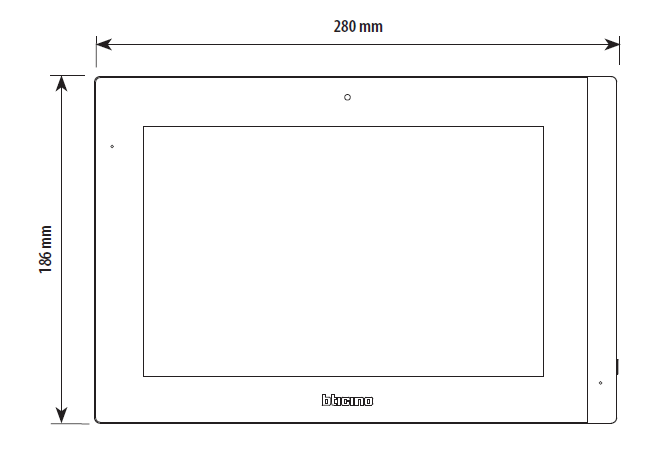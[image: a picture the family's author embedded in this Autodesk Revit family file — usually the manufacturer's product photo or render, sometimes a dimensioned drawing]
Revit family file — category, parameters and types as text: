
# Revit family: Legrand-Hotel_UX_ONE-Thermostat-Avec Service
name_source: partatom
category: Equipement électrique
units: mm (PartAtom-declared; Revit-internal decimal feet)

## family parameters
Configuration du panneau = Deux colonnes, circuits au sein
Cote de connecteur circulaire = Utiliser le diamètre
Couper avec des vides une fois chargée = Non
Hôte = Face
Partagée = Non
Point de calcul de pièce = Non
Type d'élément = Tableau de raccordement

## types (8) — shared parameters
Avec affichage = Oui
Conditions Générale d'Utilisation = https://export.legrand.com
Ecran Tactile = Oui
Elévation par défaut = 1500 mm  [stored 4.92126 ft]
Fabricant = LEGRAND
Fonction ne pas Déranger = Oui
Fonctionnement en parallèle possible = Oui
Hauteur = 93 mm  [stored 0.305118 ft]
IK = 04
IP = 20
Largeur = 129 mm  [stored 0.423228 ft]
Matière = Plastique
Réglage manuel de la valeur de consigne = Oui
Site web configurateur = https://uxforhotels.legrand.com
Système de bus radio = Oui
profondeur d'encastrement = 50 mm  [stored 0.164042 ft]

## per-type parameters (varying)
| type | Couleur | Désignation produit | Hauteur pictogrammes | Hauteur vide | Matériau plaque | Matériau écran | Mode de pose | Plaque apparente | Plaque encastrée | Profondeur | Référence / Modèle | Tension |
| Noir 230V Encastré NPD | Noir | HOTEL THERMOSTAT ENCASTRE NOIR 230V DND MUR | 0 mm  [stored 0 ft] | -40 mm  [stored -0.131234 ft] | LEGRAND_BLACK_PLASTIC | LEGRAND_BLACK_SCREEN | Encastré | Non | Oui | 52 mm | LG-048915 | 230 V AC |
| Noir 230V Apparent NPD | Noir | HOTEL THERMOSTAT SAILLIE NOIR 230V DND MUR | 16 mm | 0 mm  [stored 0 ft] | LEGRAND_BLACK_PLASTIC | LEGRAND_BLACK_SCREEN | saillie | Oui | Non | 28 mm  [stored 0.0918635 ft] | LG-048923 | 230 V AC |
| Blanc 230V Encastré NPD | Blanc | HOTEL THERMOSTAT ENCASTRE BLANC 230V DND MUR | 0 mm  [stored 0 ft] | -40 mm  [stored -0.131234 ft] | LEGRAND_WHITE_PLASTIC | LEGRAND_WHITE_SCREEN | Encastré | Non | Oui | 52 mm | LG-048924 | 230 V AC |
| Blanc 230V Apparent NPD | Blanc | HOTEL THERMOSTAT  SAILLIE BLANC 230V DND MUR | 16 mm | 0 mm  [stored 0 ft] | LEGRAND_WHITE_PLASTIC | LEGRAND_WHITE_SCREEN | saillie | Oui | Non | 28 mm  [stored 0.0918635 ft] | LG-048925 | 230 V AC |
| Noir 24V Encastré NPD | Noir | HOTEL THERMOSTAT  ENCASTRE NOIR 24V DND MUR | 0 mm  [stored 0 ft] | -40 mm  [stored -0.131234 ft] | LEGRAND_BLACK_PLASTIC | LEGRAND_BLACK_SCREEN | Encastré | Non | Oui | 52 mm | LG-048927 | 24 V |
| Noir 24V Apparent NPD | Noir | HOTEL THERMOSTAT  SAILLIE NOIR 24V DND MUR | 16 mm | 0 mm  [stored 0 ft] | LEGRAND_BLACK_PLASTIC | LEGRAND_BLACK_SCREEN | saillie | Oui | Non | 28 mm  [stored 0.0918635 ft] | LG-048928 | 24 V |
| Blanc 24V Encastré NPD | Blanc | HOTEL THERMOSTAT  ENCASTRE BLANC 24V DND MUR | 0 mm  [stored 0 ft] | -40 mm  [stored -0.131234 ft] | LEGRAND_WHITE_PLASTIC | LEGRAND_WHITE_SCREEN | Encastré | Non | Oui | 52 mm | LG-048929 | 24 V |
| Blanc 24V Apparent NPD | Blanc | HOTEL THERMOSTAT  SAILLIE BLANC 24V DND MUR | 16 mm | 0 mm  [stored 0 ft] | LEGRAND_WHITE_PLASTIC | LEGRAND_WHITE_SCREEN | saillie | Oui | Non | 28 mm  [stored 0.0918635 ft] | LG-048930 | 24 V |

note: [stored X ft] marks values corroborated as IEEE doubles in the binary element streams (Revit-internal decimal feet)
